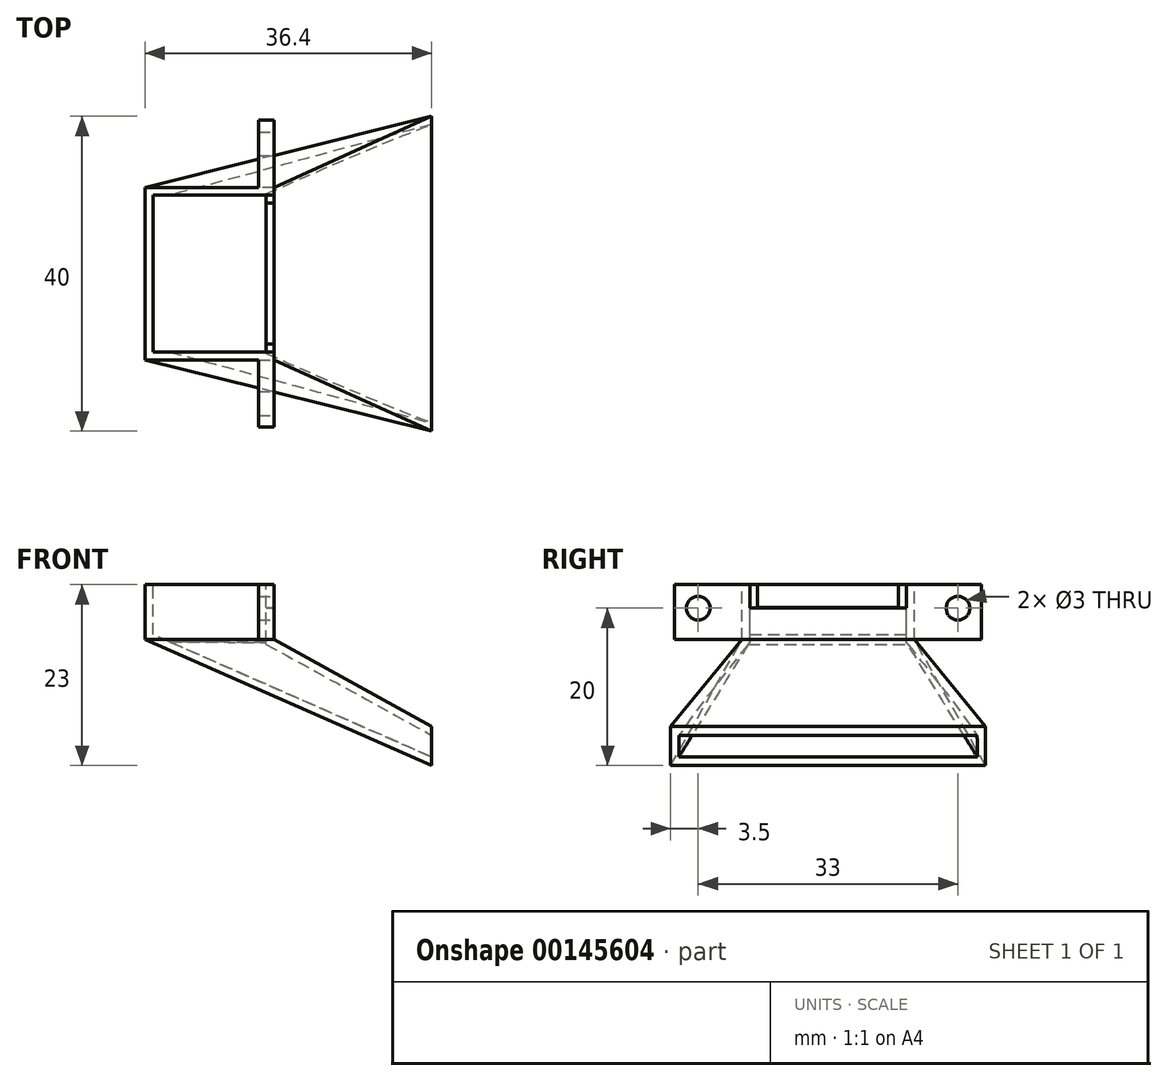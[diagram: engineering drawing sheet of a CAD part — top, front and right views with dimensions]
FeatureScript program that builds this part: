
annotation { "Feature Type Name" : "Feature", "Feature Type Description" : "" }
export const myFeature = defineFeature(function(context is Context, id is Id, definition is map)
    precondition{}
    {
        {
            assignVariable(context, id + "F0", {"name" : "fan_wide", "anyValue" : 19.9});
        }
        {
            assignVariable(context, id + "F1", {"name" : "shell", "anyValue" : 1});
        }
        {
            var Q0;
            Q0=qCreatedBy(makeId("Front.planeOp"),FACE);
            var sketch = newSketch(context, id + "F2", { "sketchPlane" : qUnion([Q0])});
            skLineSegment(sketch, "E0.bottom", {"start": v(0, 0) * mm, "end": v(-16.4, 0) * mm});
            skLineSegment(sketch, "E0.top", {"start": v(0, 7) * mm, "end": v(-16.4, 7) * mm});
            skLineSegment(sketch, "E0.left", {"start": v(0, 0) * mm, "end": v(0, 7) * mm});
            skLineSegment(sketch, "E0.right", {"start": v(-16.4, 0) * mm, "end": v(-16.4, 7) * mm});
            skLineSegment(sketch, "E1", {"start": v(-16.4, 0) * mm, "end": v(20, -16) * mm});
            skLineSegment(sketch, "E2", {"start": v(20, -16) * mm, "end": v(20, -11) * mm});
            skLineSegment(sketch, "E3", {"start": v(20, -11) * mm, "end": v(0, 0) * mm});
            skSolve(sketch);
        }
        {
            var Q0;
            Q0=makeQuery(id+"F2.imprint","IMPRINT",FACE,{"disambiguationData":[TD([[makeQuery(id+"F2.imprint","IMPRINT",EDGE,{"derivedFrom":sQuery(id+"F2.wireOp",EDGE,"E0.bottom")}),-1.0]])]});
            var Q1;
            Q1=makeQuery(id+"F2.imprint","IMPRINT",FACE,{"disambiguationData":[TD([[makeQuery(id+"F2.imprint","IMPRINT",EDGE,{"derivedFrom":sQuery(id+"F2.wireOp",EDGE,"E0.bottom")}),1.0]])]});
            extrude(context, id + "F3", {"entities" : qUnion([Q0, Q1]), "depth" : (getVariable(context, 'fan_wide') + 2 * getVariable(context, 'shell')) * mm, "offsetDistance" : 25 * mm});
        }
        {
            var Q0;
            Q0=qCreatedBy(makeId("Top.planeOp"),FACE);
            var sketch = newSketch(context, id + "F4", { "sketchPlane" : qUnion([Q0])});
            skLineSegment(sketch, "E4.0.0", {"start": v(0, 0) * mm, "end": v(-16.4, 0) * mm});
            skLineSegment(sketch, "E4.0.1", {"start": v(-16.4, 0) * mm, "end": v(-16.4, -21.9) * mm});
            skLineSegment(sketch, "E4.0.2", {"start": v(-16.4, -21.9) * mm, "end": v(0, -21.9) * mm});
            skLineSegment(sketch, "E4.0.3", {"start": v(0, -21.9) * mm, "end": v(0, 0) * mm});
            skSolve(sketch);
        }
        {
            var Q0;
            Q0=makeQuery(id+"F3.opExtrude","SWEPT_FACE",FACE,{"disambiguationData":[OSD([sQuery(id+"F2.wireOp",EDGE,"E2")])]});
            cPlane(context, id + "F5", {"entities" : qUnion([Q0]), "cplaneType" : CPlaneType.OFFSET, "offset" : 0 * mm, "width" : 150 * mm, "height" : 150 * mm});
        }
        {
            var Q0;
            Q0=qCreatedBy(id+"F5.planeOp",FACE);
            var sketch = newSketch(context, id + "F6", { "sketchPlane" : qUnion([Q0])});
            skLineSegment(sketch, "E5.0.0", {"start": v(0, -16) * mm, "end": v(0, -11) * mm, "construction": true});
            skLineSegment(sketch, "E5.0.1", {"start": v(0, -11) * mm, "end": v(-21.9, -11) * mm, "construction": true});
            skLineSegment(sketch, "E5.0.2", {"start": v(-21.9, -11) * mm, "end": v(-21.9, -16) * mm, "construction": true});
            skLineSegment(sketch, "E5.0.3", {"start": v(-21.9, -16) * mm, "end": v(0, -16) * mm, "construction": true});
            skLineSegment(sketch, "E6", {"start": v(-21.9, -11) * mm, "end": v(0, -16) * mm, "construction": true});
            skPoint(sketch, "E7", {"position": v(-10.95, -13.5) * mm});
            skLineSegment(sketch, "E8.bottom", {"start": v(9.05, -11) * mm, "end": v(-30.95, -11) * mm});
            skLineSegment(sketch, "E8.top", {"start": v(9.05, -16) * mm, "end": v(-30.95, -16) * mm});
            skLineSegment(sketch, "E8.left", {"start": v(9.05, -11) * mm, "end": v(9.05, -16) * mm});
            skLineSegment(sketch, "E8.right", {"start": v(-30.95, -11) * mm, "end": v(-30.95, -16) * mm});
            skSolve(sketch);
        }
        {
            var Q1;
            Q1=makeQuery(id+"F6.imprint","IMPRINT",FACE,{"disambiguationData":[TD([[makeQuery(id+"F6.imprint","IMPRINT",EDGE,{"derivedFrom":sQuery(id+"F6.wireOp",EDGE,"E8.bottom")}),1.0]])]});
            var Q2;
            Q2=makeQuery(id+"F4.imprint","IMPRINT",FACE,{"disambiguationData":[TD([[makeQuery(id+"F4.imprint","IMPRINT",EDGE,{"derivedFrom":sQuery(id+"F4.wireOp",EDGE,"E4.0.0")}),1.0]])]});
            loft(context, id + "F7", {"operationType" : NewBodyOperationType.ADD, "sheetProfilesArray" : [{ "sheetProfileEntities" : qUnion([Q1]) }, { "sheetProfileEntities" : qUnion([Q2]) }]});
        }
        {
            var Q0;
            Q0=makeQuery(id+"F3.opExtrude","SWEPT_FACE",FACE,{"disambiguationData":[OSD([sQuery(id+"F2.wireOp",EDGE,"E0.top")])]});
            var Q1;
            Q1=makeQuery(id+"F7.boolean.opBoolean","MERGE",FACE,{"derivedFrom":[makeQuery(id+"F3.opExtrude","SWEPT_FACE",FACE,{"disambiguationData":[OSD([sQuery(id+"F2.wireOp",EDGE,"E2")])]}),makeQuery(id+"F7.opLoft","CAP_FACE",FACE,{"disambiguationData":[OSD([makeQuery(id+"F6.imprint","IMPRINT",FACE,{"disambiguationData":[TD([[makeQuery(id+"F6.imprint","IMPRINT",EDGE,{"derivedFrom":sQuery(id+"F6.wireOp",EDGE,"E8.bottom")}),1.0]])]})])],"isStart":true})]});
            shell(context, id + "F8", {"entities" : qUnion([Q0, Q1]), "thickness" : (getVariable(context, 'shell')) * mm});
        }
        {
            var Q0;
            Q0=makeQuery(id+"F3.opExtrude","SWEPT_FACE",FACE,{"disambiguationData":[OSD([sQuery(id+"F2.wireOp",EDGE,"E0.left")])]});
            var sketch = newSketch(context, id + "F9", { "sketchPlane" : qUnion([Q0])});
            skLineSegment(sketch, "E9", {"start": v(-10.95, 7) * mm, "end": v(-10.95, 0) * mm, "construction": true});
            skLineSegment(sketch, "E10", {"start": v(-27.45, 4) * mm, "end": v(5.55, 4) * mm, "construction": true});
            skCircle(sketch, "E11", {"center": v(-27.45, 4) * mm, "radius": 1.5 * mm});
            skCircle(sketch, "E12", {"center": v(5.55, 4) * mm, "radius": 1.5 * mm});
            skLineSegment(sketch, "E13.bottom", {"start": v(8.55, 0) * mm, "end": v(-30.45, 0) * mm});
            skLineSegment(sketch, "E13.top", {"start": v(8.55, 7) * mm, "end": v(-30.45, 7) * mm});
            skLineSegment(sketch, "E13.left", {"start": v(8.55, 0) * mm, "end": v(8.55, 7) * mm});
            skLineSegment(sketch, "E13.right", {"start": v(-30.45, 0) * mm, "end": v(-30.45, 7) * mm});
            skPoint(sketch, "E13.middle", {"position": v(-10.95, 3.5) * mm});
            skLineSegment(sketch, "E14.0", {"start": v(-20.9, -0.35) * mm, "end": v(-20.9, 7) * mm, "construction": true});
            skLineSegment(sketch, "E14.1", {"start": v(-1, -0.35) * mm, "end": v(-1, 7) * mm, "construction": true});
            skLineSegment(sketch, "E15.bottom", {"start": v(-20.9, 7) * mm, "end": v(-1, 7) * mm});
            skLineSegment(sketch, "E15.top", {"start": v(-20.9, 4) * mm, "end": v(-1, 4) * mm});
            skLineSegment(sketch, "E15.left", {"start": v(-20.9, 7) * mm, "end": v(-20.9, 4) * mm});
            skLineSegment(sketch, "E15.right", {"start": v(-1, 7) * mm, "end": v(-1, 4) * mm});
            skLineSegment(sketch, "E16.bottom", {"start": v(-19.9, 7) * mm, "end": v(-2, 7) * mm});
            skLineSegment(sketch, "E16.top", {"start": v(-19.9, 4.1) * mm, "end": v(-2, 4.1) * mm});
            skLineSegment(sketch, "E16.left", {"start": v(-19.9, 7) * mm, "end": v(-19.9, 4.1) * mm});
            skLineSegment(sketch, "E16.right", {"start": v(-2, 7) * mm, "end": v(-2, 4.1) * mm});
            skSolve(sketch);
        }
        {
            var Q0;
            Q0=makeQuery(id+"F9.imprint","IMPRINT",FACE,{"disambiguationData":[TD([[makeQuery(id+"F9.imprint","IMPRINT",EDGE,{"derivedFrom":sQuery(id+"F9.wireOp",EDGE,"E12")}),-1.0]])]});
            var Q1;
            Q1=makeQuery(id+"F9.imprint","IMPRINT",FACE,{"disambiguationData":[TD([[makeQuery(id+"F9.imprint","IMPRINT",EDGE,{"derivedFrom":sQuery(id+"F9.wireOp",EDGE,"E11")}),-1.0]])]});
            extrude(context, id + "F10", {"entities" : qUnion([Q0, Q1]), "operationType" : NewBodyOperationType.ADD, "oppositeDirection" : true, "depth" : 2 * mm, "offsetDistance" : 25 * mm});
        }
        {
            var Q0;
            Q0=makeQuery(id+"F9.imprint","IMPRINT",FACE,{"disambiguationData":[TD([[makeQuery(id+"F9.imprint","IMPRINT",EDGE,{"derivedFrom":sQuery(id+"F9.wireOp",EDGE,"E15.top")}),1.0]])]});
            var Q1;
            Q1=makeQuery(id+"F9.imprint","IMPRINT",FACE,{"disambiguationData":[TD([[makeQuery(id+"F9.imprint","IMPRINT",EDGE,{"derivedFrom":sQuery(id+"F9.wireOp",EDGE,"E16.bottom")}),-1.0]])]});
            extrude(context, id + "F11", {"entities" : qUnion([Q0, Q1]), "operationType" : NewBodyOperationType.REMOVE, "oppositeDirection" : true, "depth" : 2 * mm, "offsetDistance" : 25 * mm});
        }
    });
